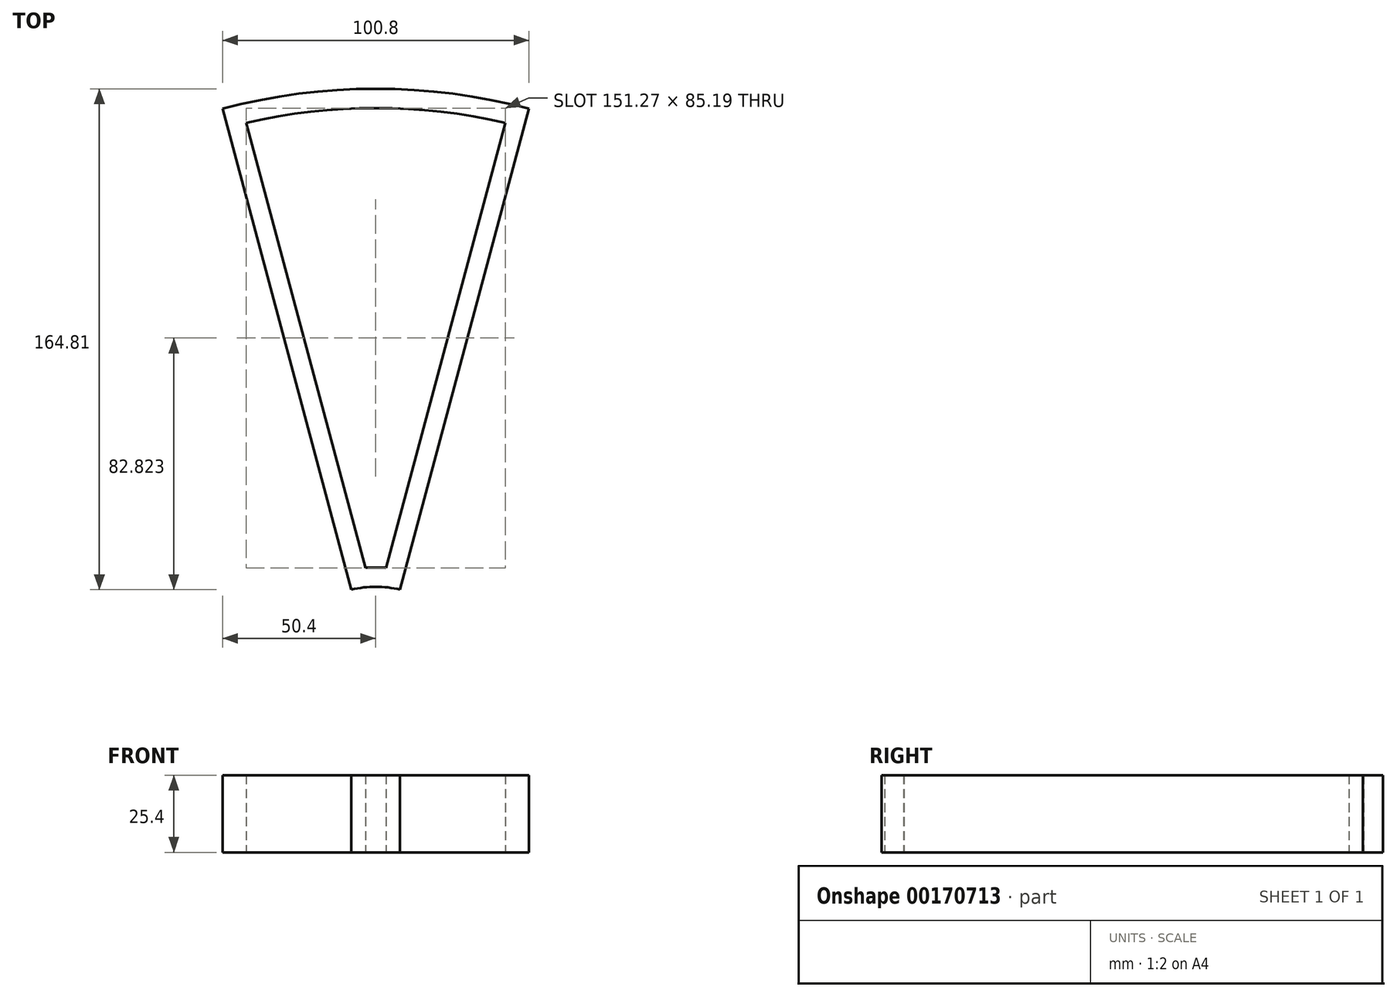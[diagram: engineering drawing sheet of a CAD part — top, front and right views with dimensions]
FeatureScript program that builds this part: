
annotation { "Feature Type Name" : "Feature", "Feature Type Description" : "" }
export const myFeature = defineFeature(function(context is Context, id is Id, definition is map)
    precondition{}
    {
        {
            var Q0;
            Q0=qCreatedBy(makeId("Top.planeOp"),FACE);
            var sketch = newSketch(context, id + "F0", { "sketchPlane" : qUnion([Q0])});
            skArc(sketch, "E0", {"start": v(8, 32.04) * mm, "mid": v(0, 33.02) * mm, "end": v(-8, 32.04) * mm});
            skArc(sketch, "E1", {"start": v(50.4, 190.29) * mm, "mid": v(0, 196.85) * mm, "end": v(-50.4, 190.29) * mm});
            skLineSegment(sketch, "E2", {"start": v(8, 32.04) * mm, "end": v(50.4, 190.29) * mm});
            skLineSegment(sketch, "E3", {"start": v(-50.4, 190.29) * mm, "end": v(-8, 32.04) * mm});
            skLineSegment(sketch, "E4", {"start": v(0, 0) * mm, "end": v(0, 96.4) * mm, "construction": true});
            skLineSegment(sketch, "E5", {"start": v(3.35, 39.23) * mm, "end": v(42.6, 185.68) * mm});
            skLineSegment(sketch, "E6", {"start": v(-42.6, 185.68) * mm, "end": v(-3.35, 39.23) * mm});
            skArc(sketch, "E7", {"start": v(-3.35, 39.23) * mm, "mid": v(0, 39.37) * mm, "end": v(3.35, 39.23) * mm});
            skArc(sketch, "E8", {"start": v(42.6, 185.68) * mm, "mid": v(0, 190.5) * mm, "end": v(-42.6, 185.68) * mm});
            skSolve(sketch);
        }
        {
            var Q0;
            Q0=makeQuery(id+"F0.imprint","IMPRINT",FACE,{"disambiguationData":[TD([[makeQuery(id+"F0.imprint","IMPRINT",EDGE,{"derivedFrom":sQuery(id+"F0.wireOp",EDGE,"E0")}),-1.0]])]});
            extrude(context, id + "F1", {"entities" : qUnion([Q0]), "depth" : 25.4 * mm});
        }
    });
